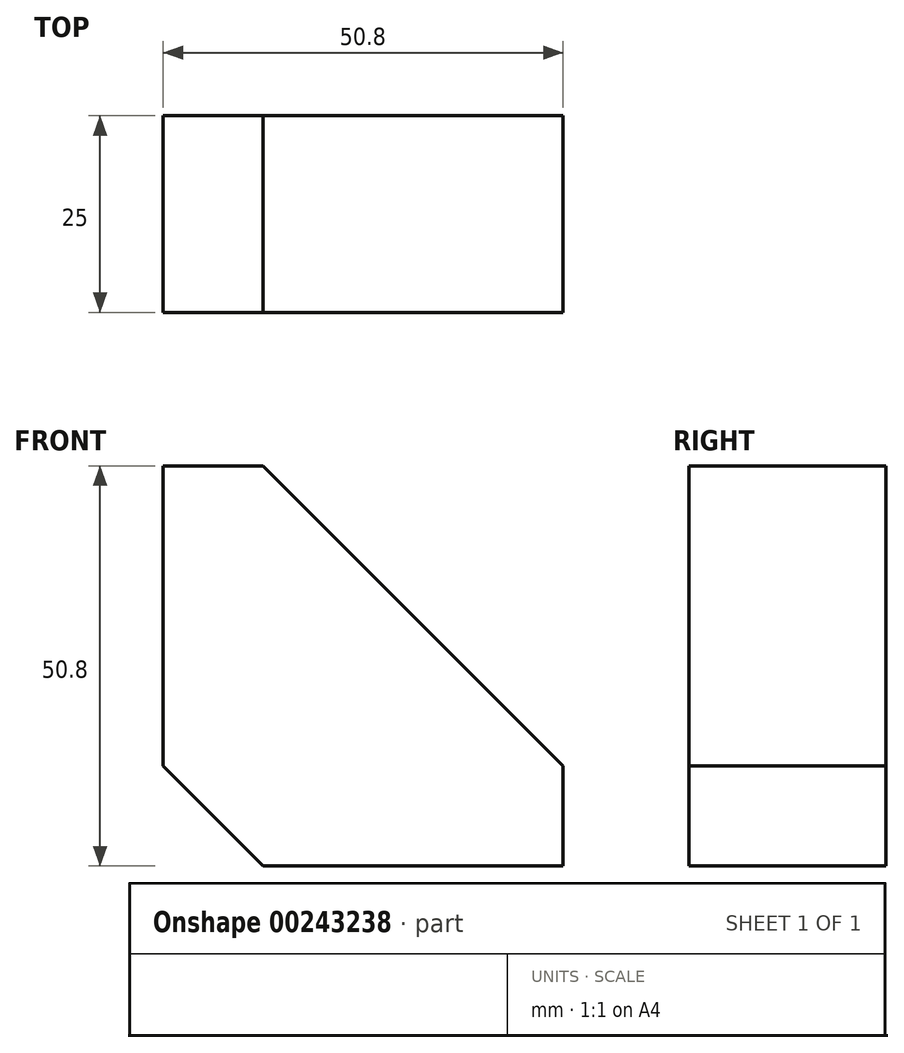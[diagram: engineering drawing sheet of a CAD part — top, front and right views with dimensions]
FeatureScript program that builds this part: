
annotation { "Feature Type Name" : "Feature", "Feature Type Description" : "" }
export const myFeature = defineFeature(function(context is Context, id is Id, definition is map)
    precondition{}
    {
        {
            var Q0;
            Q0=qCreatedBy(makeId("Front.planeOp"),FACE);
            var sketch = newSketch(context, id + "F0", { "sketchPlane" : qUnion([Q0])});
            skLineSegment(sketch, "E0", {"start": v(-23.15, 22.83) * mm, "end": v(-10.45, 22.83) * mm});
            skLineSegment(sketch, "E1", {"start": v(27.65, -27.97) * mm, "end": v(-10.45, -27.97) * mm});
            skLineSegment(sketch, "E2", {"start": v(-10.45, -27.97) * mm, "end": v(-23.15, -15.27) * mm});
            skLineSegment(sketch, "E3", {"start": v(-23.15, -15.27) * mm, "end": v(-23.15, 22.83) * mm});
            skLineSegment(sketch, "E4", {"start": v(27.65, -27.97) * mm, "end": v(27.65, -15.27) * mm});
            skLineSegment(sketch, "E5", {"start": v(27.65, -15.27) * mm, "end": v(-10.45, 22.83) * mm});
            skSolve(sketch);
        }
        {
            var Q0;
            Q0 = qSketchRegion(id + "F0", true);
            extrude(context, id + "F1", {"entities" : qUnion([Q0]), "endBound" : BoundingType.SYMMETRIC, "depth" : 25 * mm});
        }
    });
